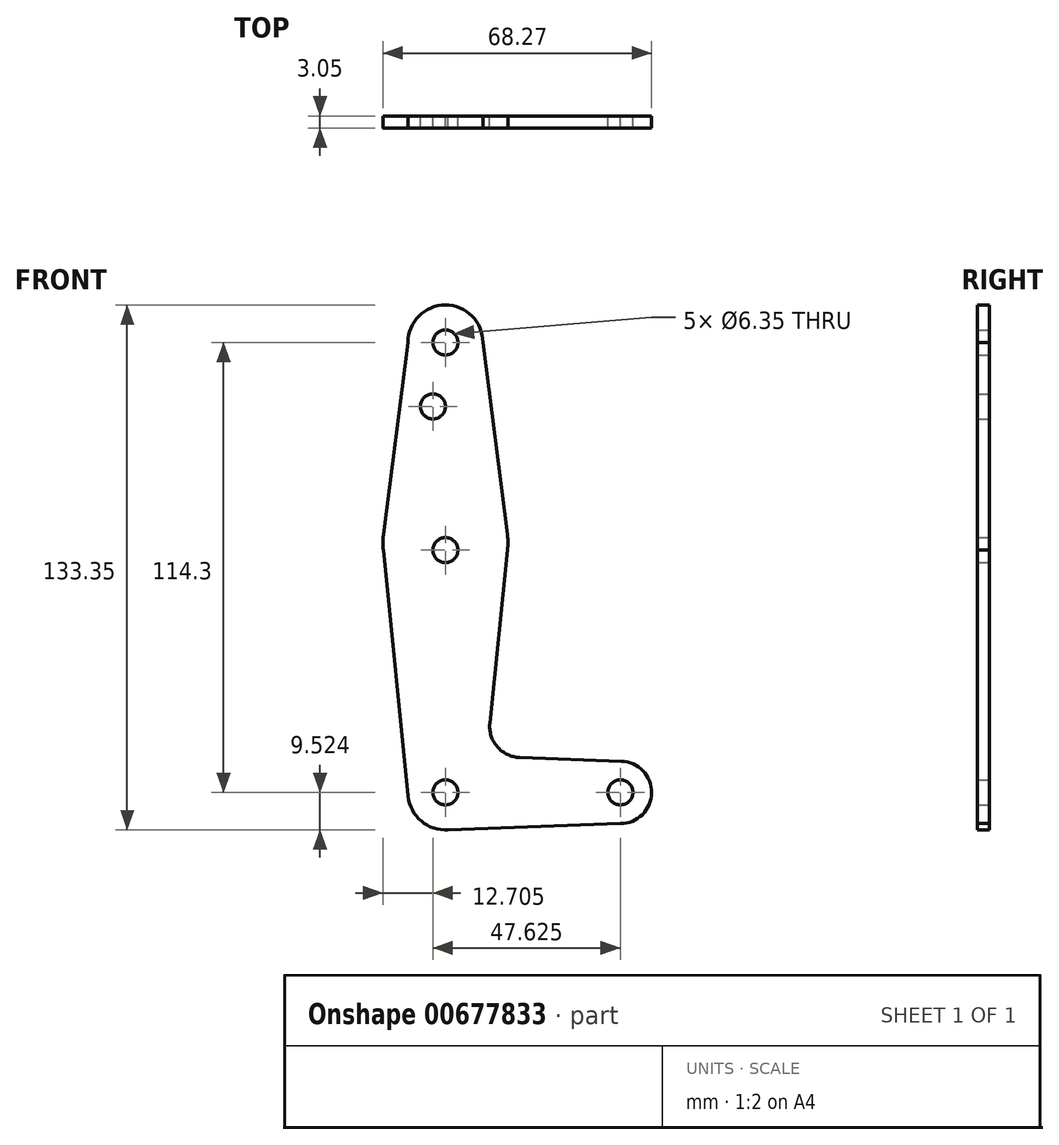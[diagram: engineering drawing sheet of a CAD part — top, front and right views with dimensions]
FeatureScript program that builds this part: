
annotation { "Feature Type Name" : "Feature", "Feature Type Description" : "" }
export const myFeature = defineFeature(function(context is Context, id is Id, definition is map)
    precondition{}
    {
        {
            var Q0;
            Q0=qCreatedBy(makeId("Front.planeOp"),FACE);
            var sketch = newSketch(context, id + "F0", { "sketchPlane" : qUnion([Q0])});
            skLineSegment(sketch, "E0", {"start": v(0, -61.55) * mm, "end": v(0, 52.75) * mm});
            skLineSegment(sketch, "E1", {"start": v(0, -61.55) * mm, "end": v(0, 1.95) * mm});
            skCircle(sketch, "E2", {"center": v(0, 52.75) * mm, "radius": 9.53 * mm});
            skCircle(sketch, "E3", {"center": v(0, 1.95) * mm, "radius": 15.88 * mm});
            skCircle(sketch, "E4", {"center": v(0, -61.55) * mm, "radius": 9.53 * mm});
            skCircle(sketch, "E5", {"center": v(44.45, -61.55) * mm, "radius": 7.94 * mm});
            skLineSegment(sketch, "E6", {"start": v(9.53, 52.75) * mm, "end": v(15.75, 3.96) * mm});
            skLineSegment(sketch, "E7", {"start": v(-9.53, 52.75) * mm, "end": v(-15.75, 3.96) * mm});
            skLineSegment(sketch, "E8", {"start": v(-15.75, 0) * mm, "end": v(-9.48, -62.5) * mm});
            skLineSegment(sketch, "E9", {"start": v(0, 0) * mm, "end": v(0, 36.53) * mm});
            skLineSegment(sketch, "E10", {"start": v(0, 36.53) * mm, "end": v(-3.17, 36.53) * mm});
            skCircle(sketch, "E11", {"center": v(-3.17, 36.53) * mm, "radius": 3.17 * mm});
            skCircle(sketch, "E12", {"center": v(0, 0) * mm, "radius": 3.18 * mm});
            skCircle(sketch, "E13", {"center": v(0, -61.55) * mm, "radius": 3.18 * mm});
            skCircle(sketch, "E14", {"center": v(0, 52.75) * mm, "radius": 3.18 * mm});
            skCircle(sketch, "E15", {"center": v(44.45, -61.55) * mm, "radius": 3.18 * mm});
            skLineSegment(sketch, "E16", {"start": v(0, -71.07) * mm, "end": v(44.45, -69.48) * mm});
            skLineSegment(sketch, "E17", {"start": v(15.75, 0) * mm, "end": v(11.27, -43.94) * mm});
            skLineSegment(sketch, "E18", {"start": v(18.9, -52.7) * mm, "end": v(44.73, -53.61) * mm});
            skArc(sketch, "E19.filletArc", {"start": v(11.27, -43.94) * mm, "mid": v(13.18, -49.97) * mm, "end": v(18.9, -52.7) * mm});
            skSolve(sketch);
        }
        {
            var Q0;
            Q0 = qSketchRegion(id + "F0", true);
            extrude(context, id + "F1", {"entities" : qUnion([Q0]), "depth" : 3.05 * mm, "offsetDistance" : 25.4 * mm});
        }
    });
